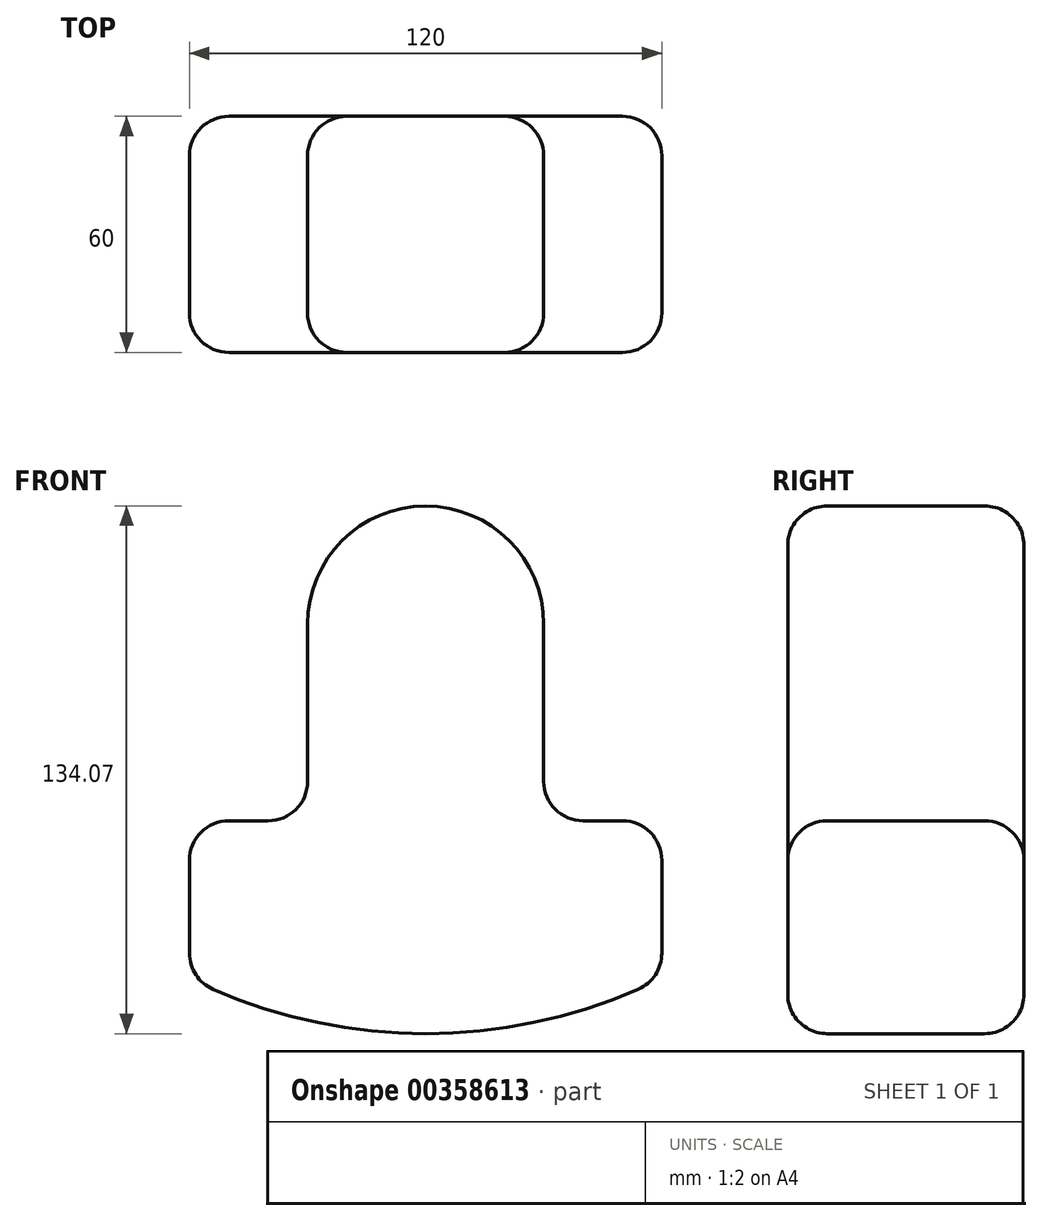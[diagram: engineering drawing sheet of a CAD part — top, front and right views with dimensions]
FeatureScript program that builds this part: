
annotation { "Feature Type Name" : "Feature", "Feature Type Description" : "" }
export const myFeature = defineFeature(function(context is Context, id is Id, definition is map)
    precondition{}
    {
        {
            var Q0;
            Q0=qCreatedBy(makeId("Front.planeOp"),FACE);
            var sketch = newSketch(context, id + "F0", { "sketchPlane" : qUnion([Q0])});
            skLineSegment(sketch, "E0.top", {"start": v(30, 75) * mm, "end": v(-30, 75) * mm});
            skLineSegment(sketch, "E0.left", {"start": v(30, -5) * mm, "end": v(30, 75) * mm});
            skLineSegment(sketch, "E0.right", {"start": v(-30, -5) * mm, "end": v(-30, 75) * mm});
            skPoint(sketch, "E0.middle", {"position": v(0, 0) * mm});
            skLineSegment(sketch, "E1.top", {"start": v(60, -5) * mm, "end": v(30, -5) * mm});
            skLineSegment(sketch, "E1.left", {"start": v(60, -45) * mm, "end": v(60, -5) * mm});
            skLineSegment(sketch, "E1.right", {"start": v(-60, -45) * mm, "end": v(-60, -5) * mm});
            skPoint(sketch, "E1.middle", {"position": v(0, -25) * mm});
            skLineSegment(sketch, "E2.trimOffspring", {"start": v(-30, -5) * mm, "end": v(-60, -5) * mm});
            skArc(sketch, "E3", {"start": v(-60, -45) * mm, "mid": v(0, -59.07) * mm, "end": v(60, -45) * mm});
            skSolve(sketch);
        }
        {
            var Q0;
            Q0=makeQuery(id+"F0.imprint","IMPRINT",FACE,{"disambiguationData":[TD([[makeQuery(id+"F0.imprint","IMPRINT",EDGE,{"derivedFrom":sQuery(id+"F0.wireOp",EDGE,"E0.top")}),1.0]])]});
            extrude(context, id + "F1", {"entities" : qUnion([Q0]), "endBound" : BoundingType.SYMMETRIC, "oppositeDirection" : true, "depth" : 60 * mm});
        }
        {
            var Q0;
            Q0=makeQuery(id+"F1.opExtrude","SWEPT_EDGE",EDGE,{"disambiguationData":[OSD([sQuery(id+"F0.wireOp",EDGE,"E0.top"),sQuery(id+"F0.wireOp",EDGE,"E0.left")])]});
            var Q1;
            Q1=makeQuery(id+"F1.opExtrude","SWEPT_EDGE",EDGE,{"disambiguationData":[OSD([sQuery(id+"F0.wireOp",EDGE,"E0.top"),sQuery(id+"F0.wireOp",EDGE,"E0.right")])]});
            fillet(context, id + "F2", {"entities" : qUnion([Q0, Q1]), "radius" : 30 * mm, "tangentPropagation" : true, "allowEdgeOverflow" : false});
        }
        {
            var Q0;
            Q0=makeQuery(id+"F1.opExtrude","CAP_FACE",FACE,{"disambiguationData":[OSD([sQuery(id+"F0.wireOp",EDGE,"E0.top"),sQuery(id+"F0.wireOp",EDGE,"E0.left"),sQuery(id+"F0.wireOp",EDGE,"E0.right"),sQuery(id+"F0.wireOp",EDGE,"E1.top"),sQuery(id+"F0.wireOp",EDGE,"E1.left"),sQuery(id+"F0.wireOp",EDGE,"E1.right"),sQuery(id+"F0.wireOp",EDGE,"E2.trimOffspring"),sQuery(id+"F0.wireOp",EDGE,"E3")])],"isStart":true});
            var Q1;
            Q1=makeQuery(id+"F1.opExtrude","SWEPT_FACE",FACE,{"disambiguationData":[OSD([sQuery(id+"F0.wireOp",EDGE,"E0.left")])]});
            var Q2;
            Q2=makeQuery(id+"F1.opExtrude","SWEPT_FACE",FACE,{"disambiguationData":[OSD([sQuery(id+"F0.wireOp",EDGE,"E1.left")])]});
            var Q3;
            Q3=makeQuery(id+"F1.opExtrude","SWEPT_FACE",FACE,{"disambiguationData":[OSD([sQuery(id+"F0.wireOp",EDGE,"E2.trimOffspring")])]});
            var Q4;
            Q4=makeQuery(id+"F1.opExtrude","CAP_FACE",FACE,{"disambiguationData":[OSD([sQuery(id+"F0.wireOp",EDGE,"E0.top"),sQuery(id+"F0.wireOp",EDGE,"E0.left"),sQuery(id+"F0.wireOp",EDGE,"E0.right"),sQuery(id+"F0.wireOp",EDGE,"E1.top"),sQuery(id+"F0.wireOp",EDGE,"E1.left"),sQuery(id+"F0.wireOp",EDGE,"E1.right"),sQuery(id+"F0.wireOp",EDGE,"E2.trimOffspring"),sQuery(id+"F0.wireOp",EDGE,"E3")])],"isStart":false});
            var Q5;
            Q5=makeQuery(id+"F1.opExtrude","SWEPT_FACE",FACE,{"disambiguationData":[OSD([sQuery(id+"F0.wireOp",EDGE,"E3")])]});
            fillet(context, id + "F3", {"entities" : qUnion([Q0, Q1, Q2, Q3, Q4, Q5]), "radius" : 10 * mm, "tangentPropagation" : true, "allowEdgeOverflow" : false});
        }
    });
